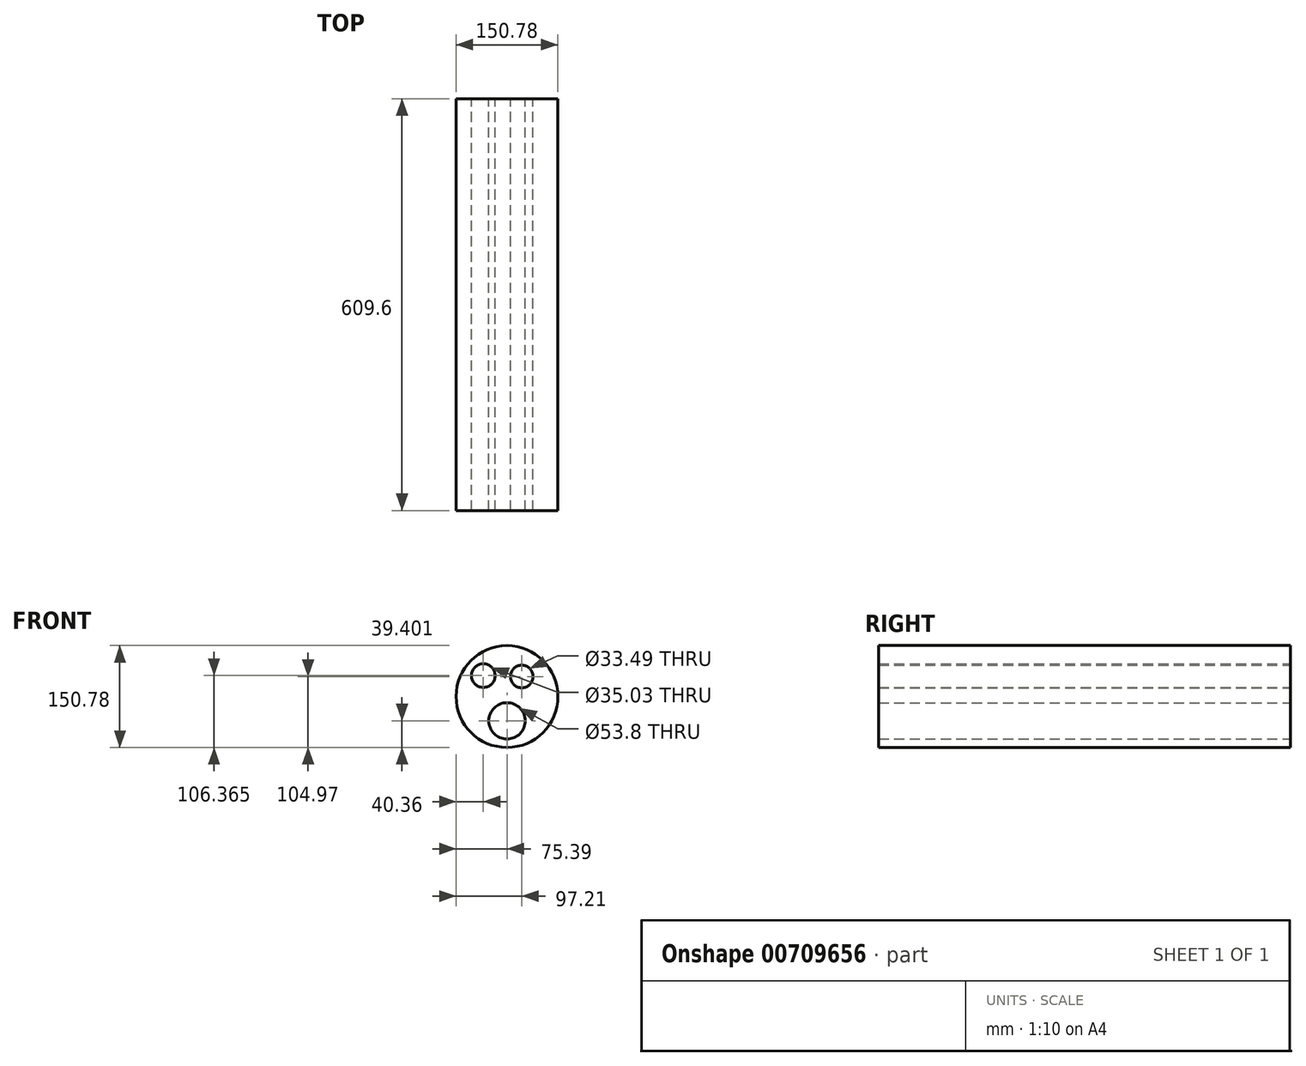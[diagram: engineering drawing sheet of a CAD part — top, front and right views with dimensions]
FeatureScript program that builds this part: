
annotation { "Feature Type Name" : "Feature", "Feature Type Description" : "" }
export const myFeature = defineFeature(function(context is Context, id is Id, definition is map)
    precondition{}
    {
        {
            var Q0;
            Q0=qCreatedBy(makeId("Front.planeOp"),FACE);
            var sketch = newSketch(context, id + "F0", { "sketchPlane" : qUnion([Q0])});
            skCircle(sketch, "E0", {"center": v(0, 0) * mm, "radius": 75.4 * mm});
            skCircle(sketch, "E1", {"center": v(21.82, 29.58) * mm, "radius": 16.74 * mm});
            skCircle(sketch, "E2", {"center": v(-35.03, 30.97) * mm, "radius": 17.52 * mm});
            skCircle(sketch, "E3", {"center": v(0, -35.99) * mm, "radius": 26.9 * mm});
            skSolve(sketch);
        }
        {
            var Q0;
            Q0=makeQuery(id+"F0.imprint","IMPRINT",FACE,{"disambiguationData":[TD([[makeQuery(id+"F0.imprint","IMPRINT",EDGE,{"derivedFrom":sQuery(id+"F0.wireOp",EDGE,"E0")}),1.0]])]});
            extrude(context, id + "F1", {"entities" : qUnion([Q0]), "depth" : 609.6 * mm, "offsetDistance" : 25.4 * mm});
        }
    });
